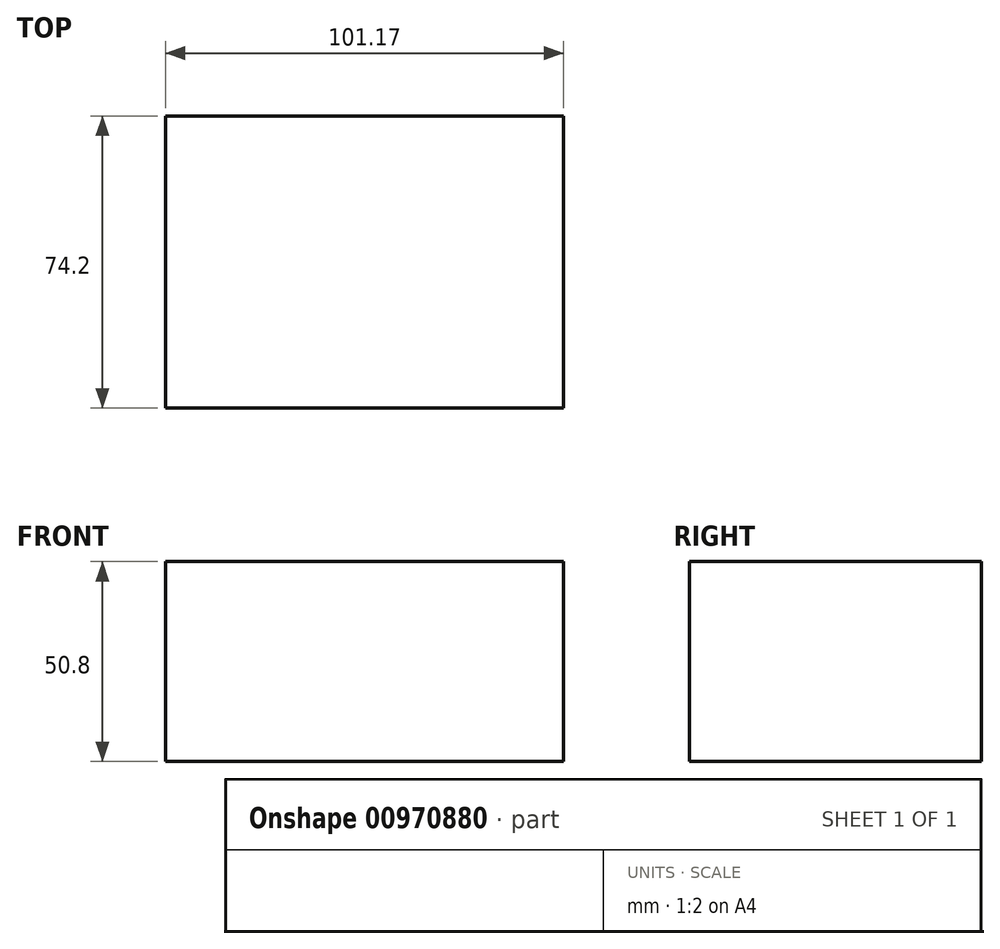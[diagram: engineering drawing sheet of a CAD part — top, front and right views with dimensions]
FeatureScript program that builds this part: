
annotation { "Feature Type Name" : "Feature", "Feature Type Description" : "" }
export const myFeature = defineFeature(function(context is Context, id is Id, definition is map)
    precondition{}
    {
        {
            var Q0;
            Q0=qCreatedBy(makeId("Top.planeOp"),FACE);
            var sketch = newSketch(context, id + "F0", { "sketchPlane" : qUnion([Q0])});
            skLineSegment(sketch, "E0.bottom", {"start": v(-38.5, 17.1) * mm, "end": v(62.68, 17.1) * mm});
            skLineSegment(sketch, "E0.top", {"start": v(-38.5, -57.1) * mm, "end": v(62.68, -57.1) * mm});
            skLineSegment(sketch, "E0.left", {"start": v(-38.5, 17.1) * mm, "end": v(-38.5, -57.1) * mm});
            skLineSegment(sketch, "E0.right", {"start": v(62.68, 17.1) * mm, "end": v(62.68, -57.1) * mm});
            skSolve(sketch);
        }
        {
            var Q0;
            Q0 = qSketchRegion(id + "F0", true);
            extrude(context, id + "F1", {"entities" : qUnion([Q0]), "depth" : 25.4 * mm, "offsetDistance" : 25.4 * mm});
        }
        {
            var Q0;
            Q0=qCreatedBy(makeId("Top.planeOp"),FACE);
            var sketch = newSketch(context, id + "F2", { "sketchPlane" : qUnion([Q0])});
            skCircle(sketch, "E1", {"center": v(0, -17.33) * mm, "radius": 19.17 * mm});
            skSolve(sketch);
        }
        {
            var Q0;
            Q0=makeQuery(id+"F1.opExtrude","CAP_FACE",FACE,{"disambiguationData":[OSD([sQuery(id+"F0.wireOp",EDGE,"E0.bottom"),sQuery(id+"F0.wireOp",EDGE,"E0.top"),sQuery(id+"F0.wireOp",EDGE,"E0.left"),sQuery(id+"F0.wireOp",EDGE,"E0.right")])],"isStart":false});
            var Q1;
            Q1=makeQuery(id+"F2.imprint","IMPRINT",FACE,{"disambiguationData":[TD([[makeQuery(id+"F2.imprint","IMPRINT",EDGE,{"derivedFrom":sQuery(id+"F2.wireOp",EDGE,"E1")}),1.0]])]});
            var Q2;
            Q2=makeQuery(id+"F1.opExtrude","CAP_FACE",FACE,{"disambiguationData":[OSD([sQuery(id+"F0.wireOp",EDGE,"E0.bottom"),sQuery(id+"F0.wireOp",EDGE,"E0.top"),sQuery(id+"F0.wireOp",EDGE,"E0.left"),sQuery(id+"F0.wireOp",EDGE,"E0.right")])],"isStart":true});
            var Q3;
            Q3=sQuery(id+"F2.wireOp",EDGE,"E1");
            extrude(context, id + "F3", {"entities" : qUnion([Q0, Q1, Q2]), "operationType" : NewBodyOperationType.ADD, "surfaceEntities" : qUnion([Q3]), "depth" : 25.4 * mm, "offsetDistance" : 25.4 * mm});
        }
    });
